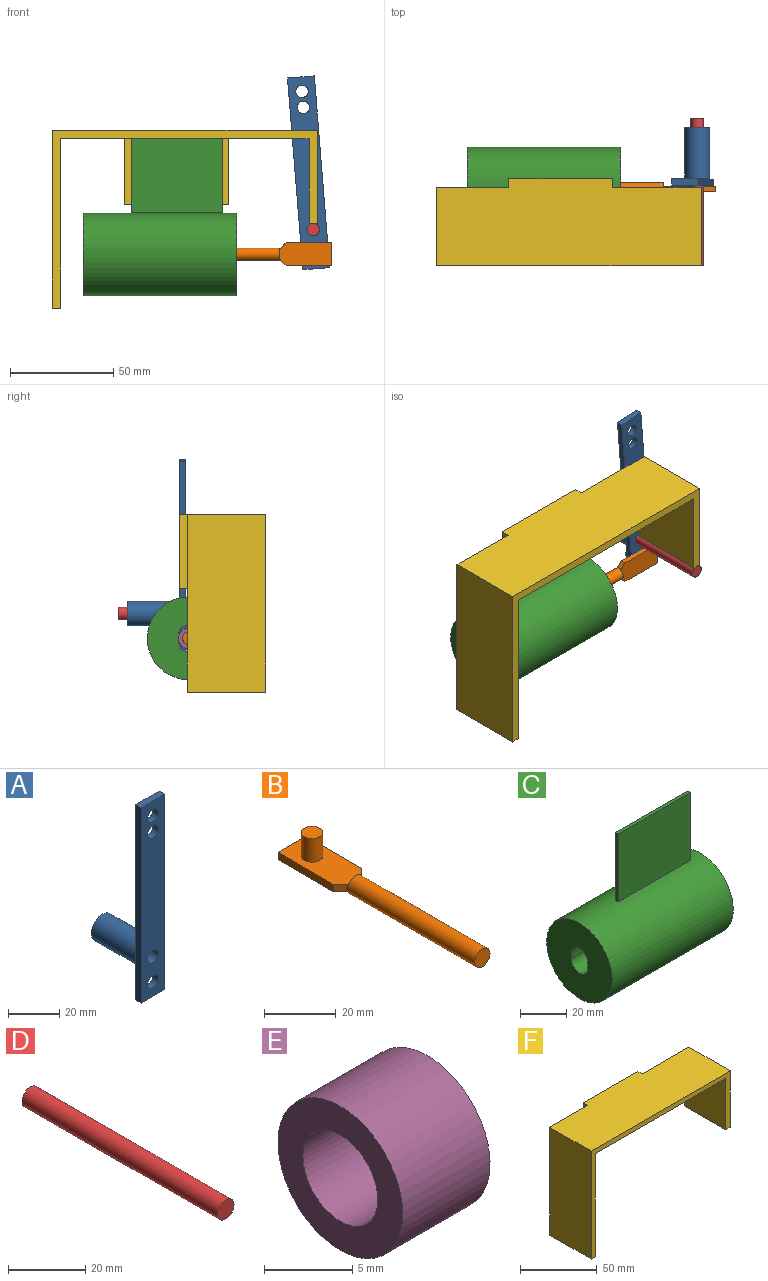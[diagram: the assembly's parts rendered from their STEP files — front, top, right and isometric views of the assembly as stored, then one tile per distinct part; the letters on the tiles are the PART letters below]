
ASSEMBLY  parts=6 mates=6
PART A: 12 faces, bbox 13x28x93 mm
  f0: plane 93x3mm, normal (1,0,0), area 279mm2, adj f1,f6,f8,f9
  f1: plane 13x3mm, normal (0,0,1), area 39mm2, adj f0,f2,f8,f9
  f2: plane 93x3mm, normal (-1,0,0), area 279mm2, adj f1,f6,f8,f9
  f3: cylinder r=3mm len=6mm, axis (0,1,0), area 56.5mm2, adj f8,f9
  f4: cylinder r=3mm len=6mm, axis (0,1,0), area 56.5mm2, adj f8,f9
  f5: cylinder r=3mm len=6mm, axis (0,1,0), area 56.5mm2, adj f8,f9
  f6: plane 13x3mm, normal (0,0,-1), area 39mm2, adj f0,f2,f8,f9
  f7: cylinder r=3mm len=28mm, axis (0,1,0), area 527.8mm2, adj f8,f11
  f8: plane 93x13mm, normal (0,-1,0), area 1095.9mm2, adj f0,f1,f2,f3,f4,f5,f6,f7
  f9: plane 93x13mm, normal (0,1,0), area 1011.1mm2, adj f0,f1,f2,f3,f4,f5,f6,f10
  f10: cylinder r=6mm len=25mm, axis (0,-1,0), area 942.5mm2, adj f9,f11
  f11: plane 12x12mm, normal (0,1,0), area 84.8mm2, adj f7,f10
PART B: 13 faces, bbox 11x75x12.3 mm
  f0: plane 5.45x1.75mm, normal (0,1,0), area 6.9mm2, adj f1,f4
  f1: cylinder r=3mm len=50.5mm, axis (0,1,0), area 944.6mm2, adj f0,f2,f3,f4,f6,f11,f12
  f2: plane 6x6mm, normal (0,-1,0), area 28.3mm2, adj f1
  f3: plane 5.45x1.75mm, normal (0,1,0), area 6.9mm2, adj f1,f6
  f4: plane 25x11mm, normal (0,0,1), area 237.8mm2, adj f0,f1,f5,f7,f8,f9,f11,f12
  f5: plane 22x2.5mm, normal (-1,0,0), area 55mm2, adj f4,f6,f8,f11
  f6: plane 25x11mm, normal (0,0,-1), area 266.1mm2, adj f1,f3,f5,f7,f8,f11,f12
  f7: plane 22x2.5mm, normal (1,0,0), area 55mm2, adj f4,f6,f8,f12
  f8: plane 11x2.5mm, normal (0,1,0), area 27.5mm2, adj f4,f5,f6,f7
  f9: cylinder r=3mm len=8mm, axis (0,0,-1), area 150.8mm2, adj f4,f10
  f10: plane 6x6mm, normal (0,0,1), area 28.3mm2, adj f9
  f11: plane 2.77x2.77mm, normal (-0.71,-0.71,0), area 9.2mm2, adj f1,f4,f5,f6
  f12: plane 2.77x2.77mm, normal (0.71,-0.71,0), area 9.2mm2, adj f1,f4,f6,f7
PART C: 12 faces, bbox 74x40x76 mm
  f0: cylinder r=20mm len=74mm, axis (-1,0,0), area 9238.4mm2, adj f5,f6,f7,f8,f10,f11
  f1: plane 74x3mm, normal (0,1,0), area 222mm2, adj f2,f4,f5,f6
  f2: cylinder r=5mm len=74mm, axis (-1,0,0), area 1162.4mm2, adj f1,f3,f5,f6
  f3: plane 74x3mm, normal (0,-1,0), area 222mm2, adj f2,f4,f5,f6
  f4: cylinder r=5mm len=74mm, axis (-1,0,0), area 1162.4mm2, adj f1,f3,f5,f6
  f5: plane 40x40mm, normal (1,0,0), area 1148.1mm2, adj f0,f1,f2,f3,f4
  f6: plane 40x40mm, normal (-1,0,0), area 1148.1mm2, adj f0,f1,f2,f3,f4
  f7: plane 44x36mm, normal (0,-1,0), area 1584mm2, adj f0,f9,f10,f11
  f8: plane 44x36mm, normal (0,1,0), area 1584mm2, adj f0,f9,f10,f11
  f9: plane 44x1.38mm, normal (0,0,1), area 60.7mm2, adj f7,f8,f10,f11
  f10: plane 36x1.38mm, normal (-1,0,0), area 49.7mm2, adj f0,f7,f8,f9
  f11: plane 36x1.38mm, normal (1,0,0), area 49.7mm2, adj f0,f7,f8,f9
PART D: 3 faces, bbox 6x71.4x6 mm
  f0: cylinder r=3mm len=71.44mm, axis (0,1,0), area 1346.6mm2, adj f1,f2
  f1: plane 6x6mm, normal (0,-1,0), area 28.3mm2, adj f0
  f2: plane 6x6mm, normal (0,1,0), area 28.3mm2, adj f0
PART E: 4 faces, bbox 7x10x10 mm
  f0: plane 10x10mm, normal (1,0,0), area 50.3mm2, adj f2,f3
  f1: plane 10x10mm, normal (-1,0,0), area 50.3mm2, adj f2,f3
  f2: cylinder r=5mm len=10mm, axis (-1,0,0), area 219.9mm2, adj f0,f1
  f3: cylinder r=3mm len=7mm, axis (-1,0,0), area 131.9mm2, adj f0,f1
PART F: 16 faces, bbox 128x42x86 mm
  f0: plane 45x43mm, normal (0,1,0), area 336mm2, adj f1,f5,f8,f9,f10,f14
  f1: plane 120x38mm, normal (0,0,-1), area 4560mm2, adj f0,f4,f6,f7,f9,f12
  f2: plane 86x38mm, normal (-1,0,0), area 3268mm2, adj f3,f5,f6,f7
  f3: plane 38x4mm, normal (0,0,-1), area 152mm2, adj f2,f4,f6,f7
  f4: plane 82x38mm, normal (1,0,0), area 3116mm2, adj f1,f3,f6,f7
  f5: plane 128x42mm, normal (0,0,1), area 5064mm2, adj f0,f2,f6,f7,f8,f11,f14,f15
  f6: plane 128x86mm, normal (0,-1,0), area 1004mm2, adj f1,f2,f3,f4,f5,f8,f9,f10
  f7: plane 86x35mm, normal (0,1,0), area 468mm2, adj f1,f2,f3,f4,f5,f15
  f8: plane 45x38mm, normal (1,0,0), area 1710mm2, adj f0,f5,f6,f10
  f9: plane 41x38mm, normal (-1,0,0), area 1558mm2, adj f0,f1,f6,f10
  f10: plane 38x4mm, normal (0,0,-1), area 152mm2, adj f0,f6,f8,f9
  f11: plane 50x36mm, normal (0,1,0), area 1800mm2, adj f5,f13,f14,f15
  f12: plane 50x32mm, normal (0,-1,0), area 1600mm2, adj f1,f13,f14,f15
  f13: plane 50x4mm, normal (0,0,-1), area 200mm2, adj f11,f12,f14,f15
  f14: plane 36x4mm, normal (1,0,0), area 144mm2, adj f0,f5,f11,f12,f13
  f15: plane 36x4mm, normal (-1,0,0), area 144mm2, adj f5,f7,f11,f12,f13
PLACE A rot(axis=(0,-1,0),4.6deg) t=(-17.44,12.54,146)mm
PLACE B rot(axis=(-0.58,-0.58,-0.58),120deg) t=(50.99,41.52,26.01)mm
PLACE C t=(19.1,-23.97,41.13)mm
PLACE D t=(-11.79,12.04,152.53)mm
PLACE E rot(axis=(1,0,0),90deg) t=(19.1,33.33,34.68)mm
PLACE F t=(-58.9,8.6,40.53)mm fixed
MATE slider B.f1 <-> E.f2  axis (1,0,0) through (26.39,7.91,66.57)mm
MATE pin_slot E.f2 <-> C.f0  axis (1,0,0) through (30.1,7.91,66.57)mm
MATE revolute A.f7 <-> D.f0  axis (0,1,0) through (67.1,37.54,78.53)mm
MATE fastened F.f12 <-> C.f8  axis (0,-1,0) through (1.1,8.6,122.53)mm
MATE fastened D.f0 <-> F.f6  axis (0,-1,0) through (67.1,-29.4,78.53)mm
MATE cylindrical A.f5 <-> B.f9  axis (0,-1,0) through (68.06,9.54,66.57)mm
